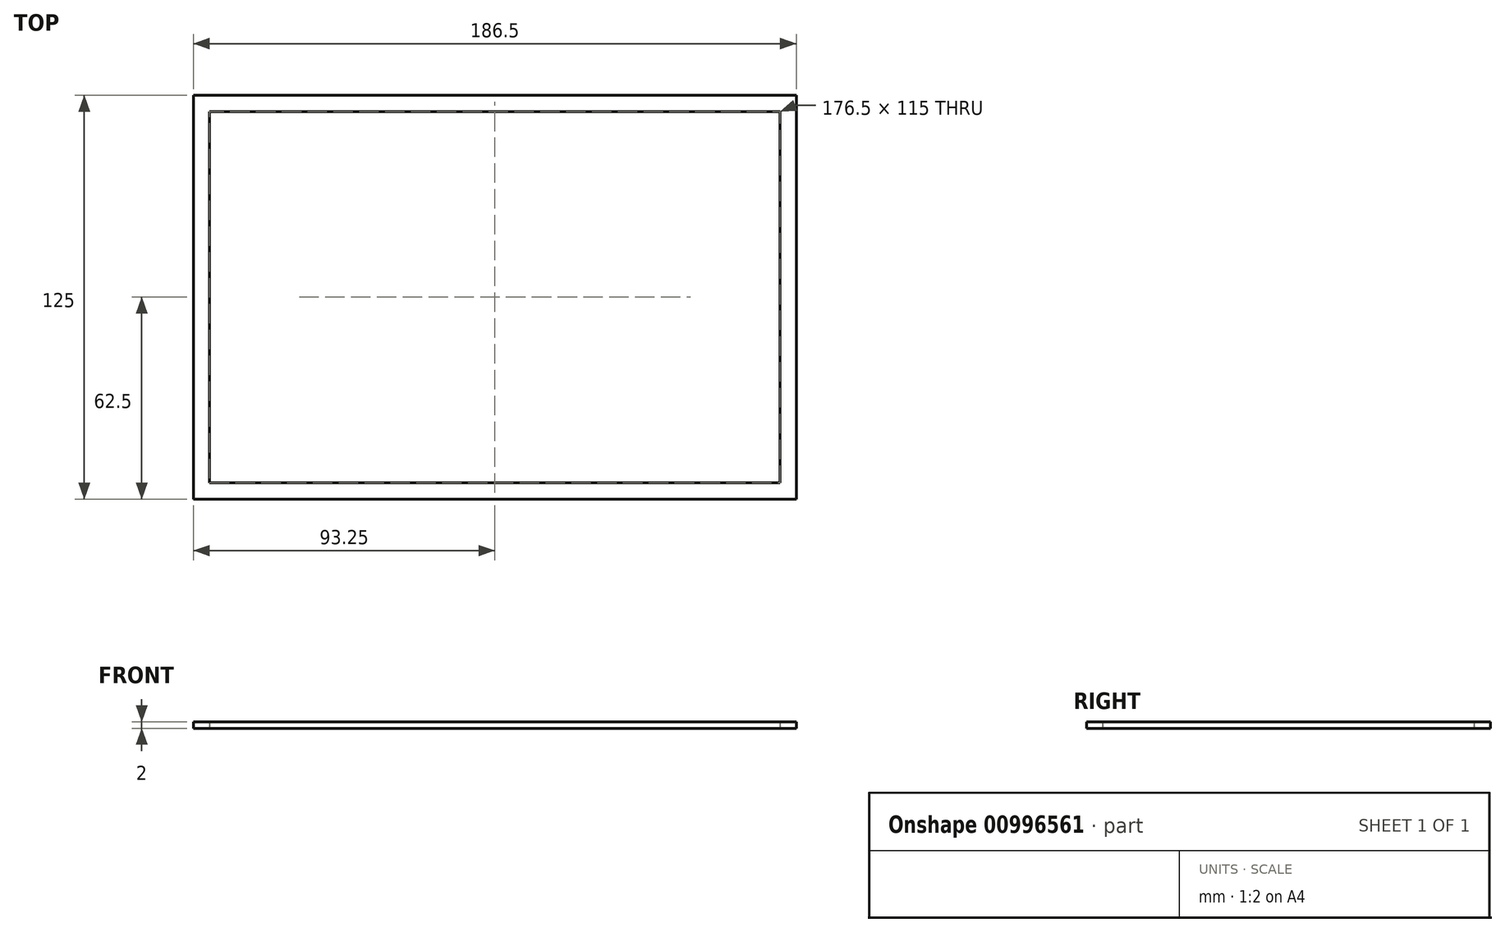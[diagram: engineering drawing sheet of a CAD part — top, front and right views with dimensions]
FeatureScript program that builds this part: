
annotation { "Feature Type Name" : "Feature", "Feature Type Description" : "" }
export const myFeature = defineFeature(function(context is Context, id is Id, definition is map)
    precondition{}
    {
        {
            var Q0;
            Q0=qCreatedBy(makeId("Top.planeOp"),FACE);
            var sketch = newSketch(context, id + "F0", { "sketchPlane" : qUnion([Q0])});
            skLineSegment(sketch, "E0.bottom", {"start": v(88.25, -57.5) * mm, "end": v(-88.25, -57.5) * mm});
            skLineSegment(sketch, "E0.top", {"start": v(88.25, 57.5) * mm, "end": v(-88.25, 57.5) * mm});
            skLineSegment(sketch, "E0.left", {"start": v(88.25, -57.5) * mm, "end": v(88.25, 57.5) * mm});
            skLineSegment(sketch, "E0.right", {"start": v(-88.25, -57.5) * mm, "end": v(-88.25, 57.5) * mm});
            skPoint(sketch, "E0.middle", {"position": v(0, 0) * mm});
            skLineSegment(sketch, "E1.0", {"start": v(93.25, 62.5) * mm, "end": v(-93.25, 62.5) * mm});
            skLineSegment(sketch, "E1.1", {"start": v(93.25, -62.5) * mm, "end": v(93.25, 62.5) * mm});
            skLineSegment(sketch, "E1.2", {"start": v(93.25, -62.5) * mm, "end": v(-93.25, -62.5) * mm});
            skLineSegment(sketch, "E1.3", {"start": v(-93.25, -62.5) * mm, "end": v(-93.25, 62.5) * mm});
            skLineSegment(sketch, "E2.bottom", {"start": v(-93.25, 62.5) * mm, "end": v(-88.25, 62.5) * mm});
            skLineSegment(sketch, "E2.top", {"start": v(-93.25, 57.5) * mm, "end": v(-88.25, 57.5) * mm});
            skLineSegment(sketch, "E2.left", {"start": v(-93.25, 62.5) * mm, "end": v(-93.25, 57.5) * mm});
            skLineSegment(sketch, "E2.right", {"start": v(-88.25, 62.5) * mm, "end": v(-88.25, 57.5) * mm});
            skSolve(sketch);
        }
        {
            var Q0;
            Q0 = qSketchRegion(id + "F0", true);
            extrude(context, id + "F1", {"entities" : qUnion([Q0]), "depth" : 2 * mm, "offsetDistance" : 25 * mm});
        }
    });
